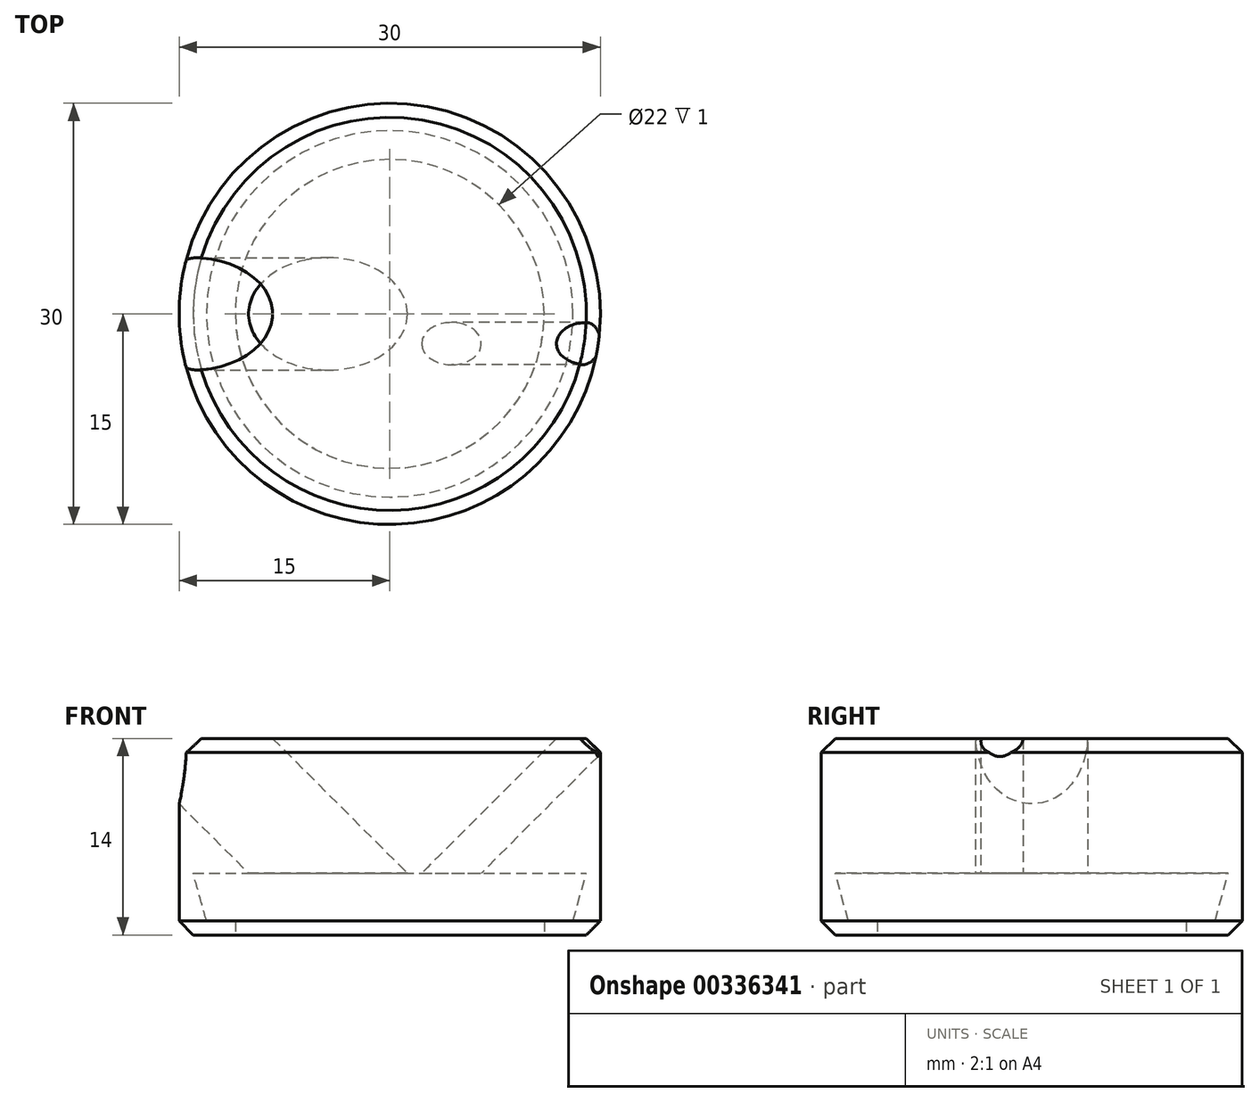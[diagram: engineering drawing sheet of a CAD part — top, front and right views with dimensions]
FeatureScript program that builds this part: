
annotation { "Feature Type Name" : "Feature", "Feature Type Description" : "" }
export const myFeature = defineFeature(function(context is Context, id is Id, definition is map)
    precondition{}
    {
        {
            var Q0;
            Q0=qCreatedBy(makeId("Top.planeOp"),FACE);
            var sketch = newSketch(context, id + "F0", { "sketchPlane" : qUnion([Q0])});
            skCircle(sketch, "E0", {"center": v(0, 0) * mm, "radius": 15 * mm});
            skSolve(sketch);
        }
        {
            var Q0;
            Q0=makeQuery(id+"F0.imprint","IMPRINT",FACE,{"disambiguationData":[TD([[makeQuery(id+"F0.imprint","IMPRINT",EDGE,{"derivedFrom":sQuery(id+"F0.wireOp",EDGE,"E0")}),1.0]])]});
            var Q1;
            Q1=qCreatedBy(makeId("Top.planeOp"),FACE);
            extrude(context, id + "F1", {"entities" : qUnion([Q0]), "endBoundEntityFace" : qUnion([Q1]), "depth" : 14 * mm});
        }
        {
            var Q0;
            Q0=makeQuery(id+"F1.opExtrude","CAP_FACE",FACE,{"disambiguationData":[OSD([sQuery(id+"F0.wireOp",EDGE,"E0")])],"isStart":false});
            var Q1;
            Q1=makeQuery(id+"F1.opExtrude","CAP_EDGE",EDGE,{"disambiguationData":[OSD([sQuery(id+"F0.wireOp",EDGE,"E0")])],"isStart":true});
            chamfer(context, id + "F2", {"entities" : qUnion([Q0, Q1]), "width" : 1 * mm, "tangentPropagation" : true});
        }
        {
            var Q0;
            Q0=qCreatedBy(makeId("Top.planeOp"),FACE);
            var sketch = newSketch(context, id + "F3", { "sketchPlane" : qUnion([Q0])});
            skCircle(sketch, "E1", {"center": v(0, 0) * mm, "radius": 11 * mm});
            skSolve(sketch);
        }
        {
            var Q0;
            Q0 = qSketchRegion(id + "F3", true);
            extrude(context, id + "F4", {"entities" : qUnion([Q0]), "operationType" : NewBodyOperationType.REMOVE, "depth" : 4.4 * mm});
        }
        {
            var Q0;
            Q0=qCreatedBy(makeId("Front.planeOp"),FACE);
            var sketch = newSketch(context, id + "F5", { "sketchPlane" : qUnion([Q0])});
            skLineSegment(sketch, "E2", {"start": v(11, 4.4) * mm, "end": v(14, 4.4) * mm});
            skLineSegment(sketch, "E3", {"start": v(14, 4.4) * mm, "end": v(13.06, 1) * mm});
            skLineSegment(sketch, "E4", {"start": v(13.06, 1) * mm, "end": v(11, 1) * mm});
            skLineSegment(sketch, "E5", {"start": v(11, 1) * mm, "end": v(11, 4.4) * mm});
            skLineSegment(sketch, "E6", {"start": v(0, 0) * mm, "end": v(0, 4.4) * mm});
            skSolve(sketch);
        }
        {
            var Q0;
            Q0=makeQuery(id+"F5.imprint","IMPRINT",FACE,{"disambiguationData":[TD([[makeQuery(id+"F5.imprint","IMPRINT",EDGE,{"derivedFrom":sQuery(id+"F5.wireOp",EDGE,"E2")}),-1.0]])]});
            var Q1;
            Q1=sQuery(id+"F5.wireOp",EDGE,"E6");
            revolve(context, id + "F6", {"operationType" : NewBodyOperationType.REMOVE, "entities" : qUnion([Q0]), "axis" : qUnion([Q1]), "revolveType" : RevolveType.FULL});
        }
        {
            var Q0;
            Q0=qCreatedBy(makeId("Top.planeOp"),FACE);
            var sketch = newSketch(context, id + "F7", { "sketchPlane" : qUnion([Q0])});
            skLineSegment(sketch, "E7", {"start": v(0, 0) * mm, "end": v(0, 6.77) * mm});
            skLineSegment(sketch, "E8", {"start": v(3, 6.77) * mm, "end": v(3, 0) * mm});
            skSolve(sketch);
        }
        {
            var Q0;
            Q0=sQuery(id+"F7.wireOp",EDGE,"E7");
            cPlane(context, id + "F8", {"entities" : qUnion([Q0]), "cplaneType" : CPlaneType.LINE_ANGLE, "offset" : 25 * mm, "angle" : 45 * degree, "oppositeDirection" : true, "width" : 150 * mm, "height" : 150 * mm});
        }
        {
            var Q0;
            Q0=qCreatedBy(id+"F8.planeOp",FACE);
            var sketch = newSketch(context, id + "F9", { "sketchPlane" : qUnion([Q0])});
            skPoint(sketch, "E9", {"position": v(0, 0) * mm});
            skSolve(sketch);
        }
        {
            var Q0;
            Q0=sQuery(id+"F9.wireOp",VERTEX,"E9");
            var Q1;
            Q1=makeQuery(id+"F1.opExtrude","SWEPT_BODY",BODY,{"disambiguationData":[OSD([sQuery(id+"F0.wireOp",EDGE,"E0")])]});
            hole(context, id + "F10", {"style" : HoleStyle.SIMPLE, "endStyle" : HoleEndStyle.THROUGH, "oppositeDirection" : true, "holeDiameter" : 8 * mm, "isTappedThrough" : true, "tappedDepth" : 12 * mm, "tapClearance" : 3, "startFromSketch" : true, "locations" : qUnion([Q0]), "scope" : qUnion([Q1])});
        }
        {
            var Q0;
            Q0=sQuery(id+"F7.wireOp",EDGE,"E8");
            cPlane(context, id + "F11", {"entities" : qUnion([Q0]), "cplaneType" : CPlaneType.LINE_ANGLE, "offset" : 25 * mm, "angle" : 45 * degree, "oppositeDirection" : true, "width" : 150 * mm, "height" : 150 * mm});
        }
        {
            var Q0;
            Q0=qCreatedBy(id+"F11.planeOp",FACE);
            var sketch = newSketch(context, id + "F12", { "sketchPlane" : qUnion([Q0])});
            skPoint(sketch, "E10", {"position": v(2.12, 0) * mm});
            skSolve(sketch);
        }
        {
            var Q0;
            Q0=sQuery(id+"F12.wireOp",VERTEX,"E10");
            var Q1;
            Q1=makeQuery(id+"F1.opExtrude","SWEPT_BODY",BODY,{"disambiguationData":[OSD([sQuery(id+"F0.wireOp",EDGE,"E0")])]});
            hole(context, id + "F13", {"style" : HoleStyle.SIMPLE, "endStyle" : HoleEndStyle.THROUGH, "holeDiameter" : 3 * mm, "isTappedThrough" : true, "tappedDepth" : 12 * mm, "tapClearance" : 3, "startFromSketch" : true, "locations" : qUnion([Q0]), "scope" : qUnion([Q1])});
        }
    });
